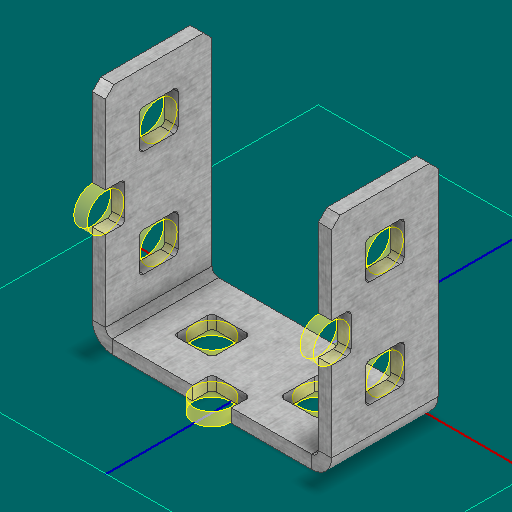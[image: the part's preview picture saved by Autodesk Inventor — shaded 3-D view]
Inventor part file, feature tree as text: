
AUTODESK INVENTOR PART (.ipt)
format: ipt  version: 2025 (Build 290162000, 162)  size: 474,624 bytes
history: native  units: in
note: dims shown in document units (in); Inventor stores cm internally (conversion verified against a paired STEP export)
features: other x173, sketch x2, sheet_metal_op x1
ambient origin geometry x8: Origin, YZ Plane, XZ Plane, XY Plane, X Axis, Y Axis, Z Axis, Center Point
bodies: Solid1 (feature_tree)
feature tree (176):
  other  "Alu C 2x2x2x1.ipt"
  other  "Solid1::Alu C 2x2x2x1.ipt"
  other  "TaggingFeature1"
  sketch  "Sketch1"  dims[d0=0.3937in]
  sketch  "Sketch2"  dims[d1=0.0625in]
  sheet_metal_op  "Body Pattern Sketch"
  other  "Arc Length"
  other  "Diagonal Plane"
  other  "Srf1"
  other  "Srf2"
  other  "Srf3"
  other  "Srf4"
  other  "Srf5"
  other  "Srf6"
  other  "Srf7"
  other  "Srf8"
  other  "Srf9"
  other  "Srf10"
  other  "Srf11"
  other  "Srf12"
  other  "Srf13"
  other  "Srf14"
  other  "Srf15"
  other  "Srf16"
  other  "Srf17"
  other  "Srf18"
  other  "Srf19"
  other  "Srf20"
  other  "Srf21"
  other  "Srf22"
  other  "Srf23"
  other  "Srf24"
  other  "Srf25"
  other  "Srf26"
  other  "Srf27"
  other  "Srf28"
  other  "Srf29"
  other  "Srf30"
  other  "Srf31"
  other  "Srf32"
  other  "Srf33"
  other  "Srf34"
  other  "Srf35"
  other  "Srf36"
  other  "Srf37"
  other  "Srf38"
  other  "Srf39"
  other  "Srf40"
  other  "Srf41"
  other  "Srf42"
  other  "Srf43"
  other  "Srf44"
  other  "Srf45"
  other  "Srf46"
  other  "Srf47"
  other  "Srf48"
  other  "Srf49"
  other  "Srf50"
  other  "Srf51"
  other  "Srf52"
  other  "Srf53"
  other  "Srf54"
  other  "Srf55"
  other  "Srf56"
  other  "Srf57"
  other  "Srf58"
  other  "Srf59"
  other  "Srf60"
  other  "Srf61"
  other  "Srf62"
  other  "Srf63"
  other  "Srf64"
  other  "Srf65"
  other  "Srf66"
  other  "Srf67"
  other  "Srf68"
  other  "Srf69"
  other  "Srf70"
  other  "Srf71"
  other  "Srf72"
  other  "Srf73"
  other  "Srf74"
  other  "Srf75"
  other  "Srf76"
  other  "Srf77"
  other  "Srf78"
  other  "Srf79"
  other  "Srf80"
  other  "Srf81"
  other  "Srf82"
  other  "Srf83"
  other  "Srf84"
  other  "Srf91::Derived"
  other  "Srf92::Derived"
  other  "Srf786::Derived"
  other  "Srf889::Derived"
  other  "Srf890::Derived"
  other  "Srf891::Derived"
  other  "Srf892::Derived"
  other  "Srf893::Derived"
  other  "Srf894::Derived"
  other  "Srf895::Derived"
  other  "Srf896::Derived"
  other  "Srf996::Derived"
  other  "Srf997::Derived"
  other  "Srf998::Derived"
  other  "Srf999::Derived"
  other  "Srf1000::Derived"
  other  "Srf1255::Derived"
  other  "Srf1256::Derived"
  other  "Srf1257::Derived"
  other  "Srf1258::Derived"
  other  "Srf1259::Derived"
  other  "Srf1315::Derived"
  other  "Srf1316::Derived"
  other  "Srf1317::Derived"
  other  "Srf1325::Derived"
  other  "Srf1326::Derived"
  other  "Srf1327::Derived"
  other  "Srf1328::Derived"
  other  "Srf1329::Derived"
  other  "Srf1330::Derived"
  other  "Srf1331::Derived"
  other  "Srf1332::Derived"
  other  "Srf1338::Derived"
  other  "Srf1339::Derived"
  other  "Srf1340::Derived"
  other  "Srf1341::Derived"
  other  "Srf1342::Derived"
  other  "Srf1369::Derived"
  other  "Srf1370::Derived"
  other  "Srf1371::Derived"
  other  "Srf1372::Derived"
  other  "Srf1373::Derived"
  other  "Srf1374::Derived"
  other  "Srf1375::Derived"
  other  "Srf1376::Derived"
  other  "Srf1384::Derived"
  other  "Srf1385::Derived"
  other  "Srf1386::Derived"
  other  "Srf1387::Derived"
  other  "Srf1388::Derived"
  other  "Srf1389::Derived"
  other  "Srf1390::Derived"
  other  "Srf1391::Derived"
  other  "Srf1397::Derived"
  other  "Srf1398::Derived"
  other  "Srf1399::Derived"
  other  "Srf1400::Derived"
  other  "Srf1401::Derived"
  other  "Srf1428::Derived"
  other  "Srf1429::Derived"
  other  "Srf1430::Derived"
  other  "Srf1431::Derived"
  other  "Srf1432::Derived"
  other  "Srf1433::Derived"
  other  "Srf1434::Derived"
  other  "Srf1473::Derived"
  other  "Srf1474::Derived"
  other  "Srf1475::Derived"
  other  "Srf1476::Derived"
  other  "Srf1477::Derived"
  other  "Srf1478::Derived"
  other  "Srf1479::Derived"
  other  "Srf1480::Derived"
  other  "Srf1481::Derived"
  other  "Srf1482::Derived"
  other  "Srf1483::Derived"
  other  "Srf1484::Derived"
  other  "Srf1485::Derived"
  other  "Srf1486::Derived"
  other  "Srf1487::Derived"
  other  "Srf1488::Derived"
  other  "Srf1489::Derived"
  other  "Srf1490::Derived"
  other  "Srf1491::Derived"
